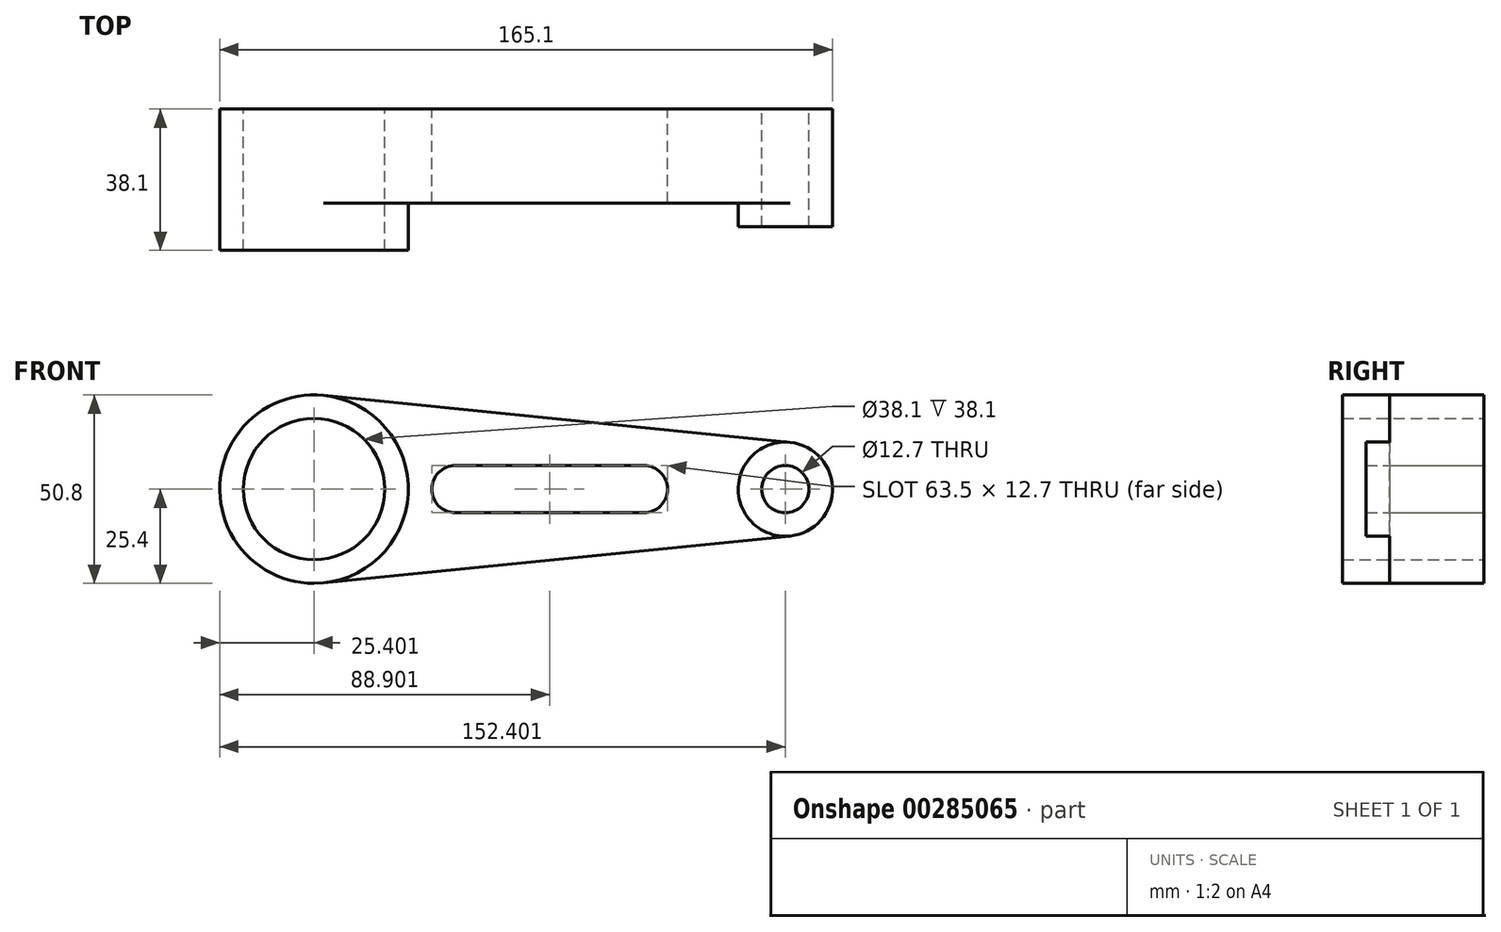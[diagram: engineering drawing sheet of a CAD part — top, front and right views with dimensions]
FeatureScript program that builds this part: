
annotation { "Feature Type Name" : "Feature", "Feature Type Description" : "" }
export const myFeature = defineFeature(function(context is Context, id is Id, definition is map)
    precondition{}
    {
        {
            var Q0;
            Q0=qCreatedBy(makeId("Front.planeOp"),FACE);
            var sketch = newSketch(context, id + "F0", { "sketchPlane" : qUnion([Q0])});
            skCircle(sketch, "E0", {"center": v(-21.47, 0) * mm, "radius": 19.05 * mm});
            skCircle(sketch, "E1", {"center": v(-21.47, 0) * mm, "radius": 25.4 * mm});
            skCircle(sketch, "E2", {"center": v(105.53, 0) * mm, "radius": 12.7 * mm});
            skCircle(sketch, "E3", {"center": v(105.53, 0) * mm, "radius": 6.35 * mm});
            skLineSegment(sketch, "E4", {"start": v(-18.93, 25.27) * mm, "end": v(106.8, 12.64) * mm});
            skLineSegment(sketch, "E5", {"start": v(-18.93, -25.27) * mm, "end": v(106.8, -12.64) * mm});
            skArc(sketch, "E6", {"start": v(67.43, -6.35) * mm, "mid": v(73.78, 0) * mm, "end": v(67.43, 6.35) * mm});
            skArc(sketch, "E7", {"start": v(16.63, 6.35) * mm, "mid": v(10.28, 0) * mm, "end": v(16.63, -6.35) * mm});
            skLineSegment(sketch, "E8", {"start": v(16.63, -6.35) * mm, "end": v(67.43, -6.35) * mm});
            skLineSegment(sketch, "E9", {"start": v(67.43, 6.35) * mm, "end": v(16.63, 6.35) * mm});
            skSolve(sketch);
        }
        {
            var Q0;
            Q0=makeQuery(id+"F0.imprint","IMPRINT",FACE,{"disambiguationData":[TD([[makeQuery(id+"F0.imprint","IMPRINT",EDGE,{"derivedFrom":sQuery(id+"F0.wireOp",EDGE,"E0")}),-1.0]])]});
            extrude(context, id + "F1", {"entities" : qUnion([Q0]), "depth" : 38.1 * mm});
        }
        {
            var Q0;
            {var subQ3=sQuery(id+"F0.wireOp",EDGE,"E4");Q0=makeQuery(id+"F0.imprint","IMPRINT",FACE,{"disambiguationData":[TD([[makeQuery(id+"F0.imprint","IMPRINT",EDGE,{"derivedFrom":subQ3}),-1.0]])]});}
            extrude(context, id + "F2", {"entities" : qUnion([Q0]), "operationType" : NewBodyOperationType.ADD, "depth" : 25.4 * mm});
        }
        {
            var Q0;
            Q0=makeQuery(id+"F0.imprint","IMPRINT",FACE,{"disambiguationData":[TD([[makeQuery(id+"F0.imprint","IMPRINT",EDGE,{"derivedFrom":sQuery(id+"F0.wireOp",EDGE,"E3")}),-1.0]])]});
            extrude(context, id + "F3", {"entities" : qUnion([Q0]), "operationType" : NewBodyOperationType.ADD, "depth" : 31.75 * mm});
        }
    });
